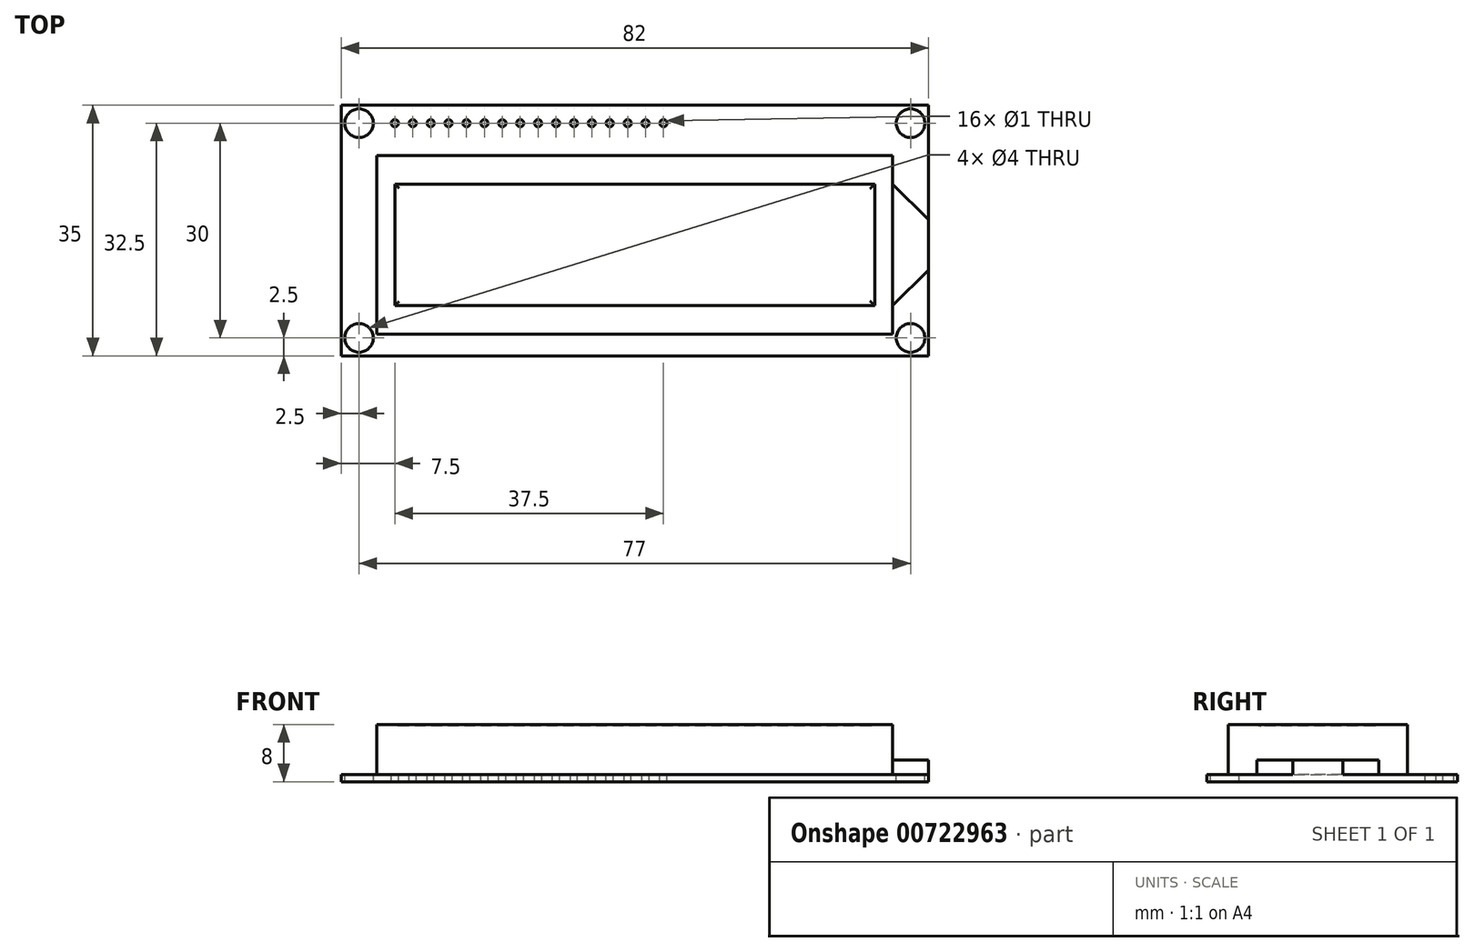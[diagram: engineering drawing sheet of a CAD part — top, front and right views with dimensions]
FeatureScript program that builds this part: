
annotation { "Feature Type Name" : "Feature", "Feature Type Description" : "" }
export const myFeature = defineFeature(function(context is Context, id is Id, definition is map)
    precondition{}
    {
        {
            var Q0;
            Q0=qCreatedBy(makeId("Top.planeOp"),FACE);
            var sketch = newSketch(context, id + "F0", { "sketchPlane" : qUnion([Q0])});
            skLineSegment(sketch, "E0.bottom", {"start": v(41, 17.5) * mm, "end": v(-41, 17.5) * mm});
            skLineSegment(sketch, "E0.top", {"start": v(41, -17.5) * mm, "end": v(-41, -17.5) * mm});
            skLineSegment(sketch, "E0.left", {"start": v(41, 17.5) * mm, "end": v(41, -17.5) * mm});
            skLineSegment(sketch, "E0.right", {"start": v(-41, 17.5) * mm, "end": v(-41, -17.5) * mm});
            skPoint(sketch, "E0.middle", {"position": v(0, 0) * mm});
            skSolve(sketch);
        }
        {
            var Q0;
            Q0 = qSketchRegion(id + "F0", true);
            extrude(context, id + "F1", {"entities" : qUnion([Q0]), "depth" : 1 * mm, "offsetDistance" : 25 * mm});
        }
        {
            var Q0;
            Q0=makeQuery(id+"F1.opExtrude","CAP_FACE",FACE,{"disambiguationData":[OSD([sQuery(id+"F0.wireOp",EDGE,"E0.bottom"),sQuery(id+"F0.wireOp",EDGE,"E0.top"),sQuery(id+"F0.wireOp",EDGE,"E0.left"),sQuery(id+"F0.wireOp",EDGE,"E0.right")])],"isStart":false});
            var sketch = newSketch(context, id + "F2", { "sketchPlane" : qUnion([Q0])});
            skLineSegment(sketch, "E1.bottom", {"start": v(-36, -14.5) * mm, "end": v(36, -14.5) * mm});
            skLineSegment(sketch, "E1.top", {"start": v(-36, 10.5) * mm, "end": v(36, 10.5) * mm});
            skLineSegment(sketch, "E1.left", {"start": v(-36, -14.5) * mm, "end": v(-36, 10.5) * mm});
            skLineSegment(sketch, "E1.right", {"start": v(36, -14.5) * mm, "end": v(36, 10.5) * mm});
            skSolve(sketch);
        }
        {
            var Q0;
            Q0 = qSketchRegion(id + "F2", true);
            extrude(context, id + "F3", {"entities" : qUnion([Q0]), "operationType" : NewBodyOperationType.ADD, "depth" : 7 * mm, "offsetDistance" : 25 * mm});
        }
        {
            var Q0;
            Q0=makeQuery(id+"F1.opExtrude","CAP_FACE",FACE,{"disambiguationData":[OSD([sQuery(id+"F0.wireOp",EDGE,"E0.bottom"),sQuery(id+"F0.wireOp",EDGE,"E0.top"),sQuery(id+"F0.wireOp",EDGE,"E0.left"),sQuery(id+"F0.wireOp",EDGE,"E0.right")])],"isStart":false});
            var sketch = newSketch(context, id + "F4", { "sketchPlane" : qUnion([Q0])});
            skLineSegment(sketch, "E2.left", {"start": v(41, -5.5) * mm, "end": v(41, 1.5) * mm});
            skLineSegment(sketch, "E3", {"start": v(36, -10.5) * mm, "end": v(41, -5.5) * mm});
            skLineSegment(sketch, "E4", {"start": v(41, 1.5) * mm, "end": v(36, 6.5) * mm});
            skLineSegment(sketch, "E5", {"start": v(36, 6.5) * mm, "end": v(36, -10.5) * mm});
            skSolve(sketch);
        }
        {
            var Q0;
            Q0 = qSketchRegion(id + "F4", true);
            extrude(context, id + "F5", {"entities" : qUnion([Q0]), "operationType" : NewBodyOperationType.ADD, "depth" : 2 * mm, "offsetDistance" : 25 * mm});
        }
        {
            var Q0;
            Q0=makeQuery(id+"F1.opExtrude","CAP_FACE",FACE,{"disambiguationData":[OSD([sQuery(id+"F0.wireOp",EDGE,"E0.bottom"),sQuery(id+"F0.wireOp",EDGE,"E0.top"),sQuery(id+"F0.wireOp",EDGE,"E0.left"),sQuery(id+"F0.wireOp",EDGE,"E0.right")])],"isStart":false});
            var sketch = newSketch(context, id + "F6", { "sketchPlane" : qUnion([Q0])});
            skCircle(sketch, "E6", {"center": v(-38.5, -15) * mm, "radius": 2 * mm});
            skCircle(sketch, "E7.MirrorC", {"center": v(38.5, -15) * mm, "radius": 2 * mm});
            skCircle(sketch, "E8.MirrorC", {"center": v(-38.5, 15) * mm, "radius": 2 * mm});
            skCircle(sketch, "E9.MirrorC", {"center": v(38.5, 15) * mm, "radius": 2 * mm});
            skSolve(sketch);
        }
        {
            var Q0;
            Q0 = qSketchRegion(id + "F6", true);
            extrude(context, id + "F7", {"entities" : qUnion([Q0]), "operationType" : NewBodyOperationType.REMOVE, "oppositeDirection" : true, "depth" : 2 * mm, "offsetDistance" : 25 * mm});
        }
        {
            var Q0;
            Q0=makeQuery(id+"F3.opExtrude","CAP_FACE",FACE,{"disambiguationData":[OSD([sQuery(id+"F2.wireOp",EDGE,"E1.bottom"),sQuery(id+"F2.wireOp",EDGE,"E1.top"),sQuery(id+"F2.wireOp",EDGE,"E1.left"),sQuery(id+"F2.wireOp",EDGE,"E1.right")])],"isStart":false});
            var sketch = newSketch(context, id + "F8", { "sketchPlane" : qUnion([Q0])});
            skLineSegment(sketch, "E10.bottom", {"start": v(33.5, 6.5) * mm, "end": v(-33.5, 6.5) * mm});
            skLineSegment(sketch, "E10.top", {"start": v(33.5, -10.5) * mm, "end": v(-33.5, -10.5) * mm});
            skLineSegment(sketch, "E10.left", {"start": v(33.5, 6.5) * mm, "end": v(33.5, -10.5) * mm});
            skLineSegment(sketch, "E10.right", {"start": v(-33.5, 6.5) * mm, "end": v(-33.5, -10.5) * mm});
            skSolve(sketch);
        }
        {
            var Q0;
            Q0 = qSketchRegion(id + "F8", true);
            extrude(context, id + "F9", {"entities" : qUnion([Q0]), "operationType" : NewBodyOperationType.REMOVE, "oppositeDirection" : true, "depth" : 0.2 * mm, "offsetDistance" : 25 * mm});
        }
        {
            var Q0;
            Q0=makeQuery(id+"F9.boolean.opBoolean","COPY",FACE,{"derivedFrom":makeQuery(id+"F9.opExtrude","CAP_FACE",FACE,{"disambiguationData":[OSD([sQuery(id+"F8.wireOp",EDGE,"E10.bottom"),sQuery(id+"F8.wireOp",EDGE,"E10.top"),sQuery(id+"F8.wireOp",EDGE,"E10.left"),sQuery(id+"F8.wireOp",EDGE,"E10.right")])],"isStart":false})});
            fillet(context, id + "F10", {"entities" : qUnion([Q0]), "radius" : 1 * mm, "tangentPropagation" : true, "allowEdgeOverflow" : false});
        }
        {
            var Q0;
            Q0=makeQuery(id+"F1.opExtrude","CAP_FACE",FACE,{"disambiguationData":[OSD([sQuery(id+"F0.wireOp",EDGE,"E0.bottom"),sQuery(id+"F0.wireOp",EDGE,"E0.top"),sQuery(id+"F0.wireOp",EDGE,"E0.left"),sQuery(id+"F0.wireOp",EDGE,"E0.right")])],"isStart":false});
            var sketch = newSketch(context, id + "F11", { "sketchPlane" : qUnion([Q0])});
            skCircle(sketch, "E11", {"center": v(-33.5, 15) * mm, "radius": 0.5 * mm});
            skCircle(sketch, "E12.1.0.0", {"center": v(-31, 15) * mm, "radius": 0.5 * mm});
            skCircle(sketch, "E12.2.0.0", {"center": v(-28.5, 15) * mm, "radius": 0.5 * mm});
            skCircle(sketch, "E12.3.0.0", {"center": v(-26, 15) * mm, "radius": 0.5 * mm});
            skCircle(sketch, "E12.4.0.0", {"center": v(-23.5, 15) * mm, "radius": 0.5 * mm});
            skCircle(sketch, "E12.5.0.0", {"center": v(-21, 15) * mm, "radius": 0.5 * mm});
            skCircle(sketch, "E12.6.0.0", {"center": v(-18.5, 15) * mm, "radius": 0.5 * mm});
            skCircle(sketch, "E12.7.0.0", {"center": v(-16, 15) * mm, "radius": 0.5 * mm});
            skCircle(sketch, "E12.8.0.0", {"center": v(-13.5, 15) * mm, "radius": 0.5 * mm});
            skCircle(sketch, "E12.9.0.0", {"center": v(-11, 15) * mm, "radius": 0.5 * mm});
            skCircle(sketch, "E12.10.0.0", {"center": v(-8.5, 15) * mm, "radius": 0.5 * mm});
            skCircle(sketch, "E12.11.0.0", {"center": v(-6, 15) * mm, "radius": 0.5 * mm});
            skCircle(sketch, "E12.12.0.0", {"center": v(-3.5, 15) * mm, "radius": 0.5 * mm});
            skCircle(sketch, "E12.13.0.0", {"center": v(-1, 15) * mm, "radius": 0.5 * mm});
            skCircle(sketch, "E12.14.0.0", {"center": v(1.5, 15) * mm, "radius": 0.5 * mm});
            skCircle(sketch, "E12.15.0.0", {"center": v(4, 15) * mm, "radius": 0.5 * mm});
            skLineSegment(sketch, "E12.direction1", {"start": v(-33.5, 15) * mm, "end": v(-31, 15) * mm, "construction": true});
            skSolve(sketch);
        }
        {
            var Q0;
            Q0 = qSketchRegion(id + "F11", true);
            extrude(context, id + "F12", {"entities" : qUnion([Q0]), "operationType" : NewBodyOperationType.REMOVE, "oppositeDirection" : true, "depth" : 2 * mm, "offsetDistance" : 25 * mm});
        }
    });
